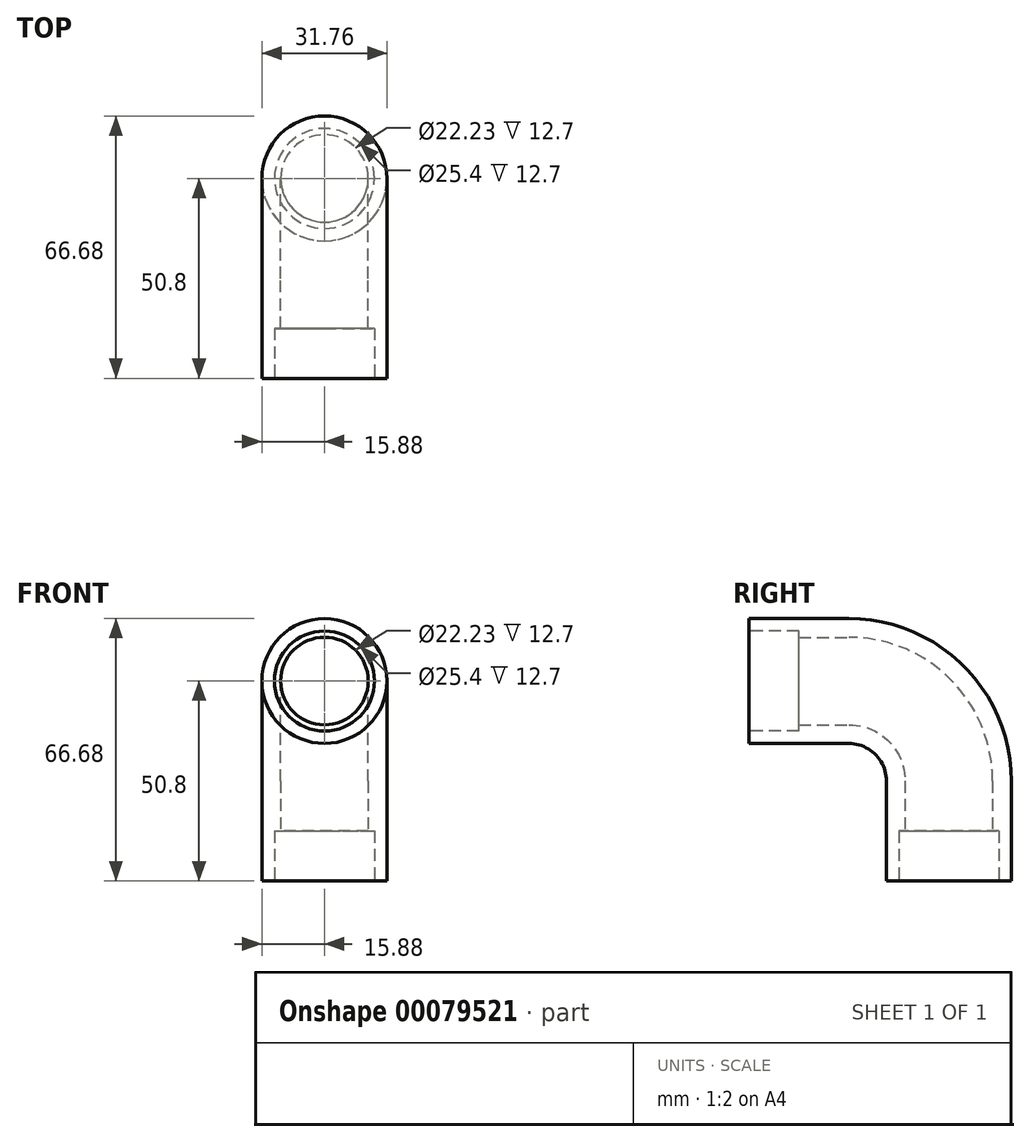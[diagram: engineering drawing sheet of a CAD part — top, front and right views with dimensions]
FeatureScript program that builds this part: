
annotation { "Feature Type Name" : "Feature", "Feature Type Description" : "" }
export const myFeature = defineFeature(function(context is Context, id is Id, definition is map)
    precondition{}
    {
        {
            var Q0;
            Q0=qCreatedBy(makeId("Front.planeOp"),FACE);
            var sketch = newSketch(context, id + "F0", { "sketchPlane" : qUnion([Q0])});
            skCircle(sketch, "E0", {"center": v(0, 0) * mm, "radius": 11.11 * mm});
            skCircle(sketch, "E1", {"center": v(0, 0) * mm, "radius": 15.88 * mm});
            skSolve(sketch);
        }
        {
            var Q0;
            Q0=qCreatedBy(makeId("Right.planeOp"),FACE);
            var sketch = newSketch(context, id + "F1", { "sketchPlane" : qUnion([Q0])});
            skLineSegment(sketch, "E2", {"start": v(0, 0) * mm, "end": v(25.4, 0) * mm});
            skLineSegment(sketch, "E3", {"start": v(50.8, -25.4) * mm, "end": v(50.8, -50.8) * mm});
            skPoint(sketch, "E4.visualSharp", {"position": v(50.8, 0) * mm});
            skArc(sketch, "E4.filletArc", {"start": v(50.8, -25.4) * mm, "mid": v(43.36, -7.44) * mm, "end": v(25.4, 0) * mm});
            skSolve(sketch);
        }
        {
            var Q0;
            Q0=makeQuery(id+"F0.imprint","IMPRINT",FACE,{"disambiguationData":[TD([[makeQuery(id+"F0.imprint","IMPRINT",EDGE,{"derivedFrom":sQuery(id+"F0.wireOp",EDGE,"E0")}),-1.0]])]});
            var Q1;
            Q1=sQuery(id+"F1.wireOp",EDGE,"E2");
            var Q2;
            Q2=sQuery(id+"F1.wireOp",EDGE,"E4.filletArc");
            var Q3;
            Q3=sQuery(id+"F1.wireOp",EDGE,"E3");
            sweep(context, id + "F2", {"profiles" : qUnion([Q0]), "path" : qUnion([Q1, Q2, Q3])});
        }
        {
            var Q0;
            Q0=qCreatedBy(makeId("Front.planeOp"),FACE);
            var sketch = newSketch(context, id + "F3", { "sketchPlane" : qUnion([Q0])});
            skCircle(sketch, "E5", {"center": v(0, 0) * mm, "radius": 12.7 * mm});
            skSolve(sketch);
        }
        {
            var Q0;
            Q0=makeQuery(id+"F3.imprint","IMPRINT",FACE,{"disambiguationData":[TD([[makeQuery(id+"F3.imprint","IMPRINT",EDGE,{"derivedFrom":sQuery(id+"F3.wireOp",EDGE,"E5")}),1.0]])]});
            extrude(context, id + "F4", {"entities" : qUnion([Q0]), "operationType" : NewBodyOperationType.REMOVE, "oppositeDirection" : true, "depth" : 12.7 * mm});
        }
        {
            var Q0;
            Q0=makeQuery(id+"F2.opSweep","CAP_FACE",FACE,{"disambiguationData":[OSD([sQuery(id+"F0.wireOp",EDGE,"E0"),sQuery(id+"F0.wireOp",EDGE,"E1"),sQuery(id+"F1.wireOp",VERTEX,"E3.end")])],"isStart":false});
            var sketch = newSketch(context, id + "F5", { "sketchPlane" : qUnion([Q0])});
            skCircle(sketch, "E6", {"center": v(0, -50.8) * mm, "radius": 12.7 * mm});
            skSolve(sketch);
        }
        {
            var Q0;
            Q0=makeQuery(id+"F5.imprint","IMPRINT",FACE,{"disambiguationData":[TD([[makeQuery(id+"F5.imprint","IMPRINT",EDGE,{"derivedFrom":sQuery(id+"F5.wireOp",EDGE,"E6")}),1.0]])]});
            extrude(context, id + "F6", {"entities" : qUnion([Q0]), "operationType" : NewBodyOperationType.REMOVE, "oppositeDirection" : true, "depth" : 12.7 * mm});
        }
    });
